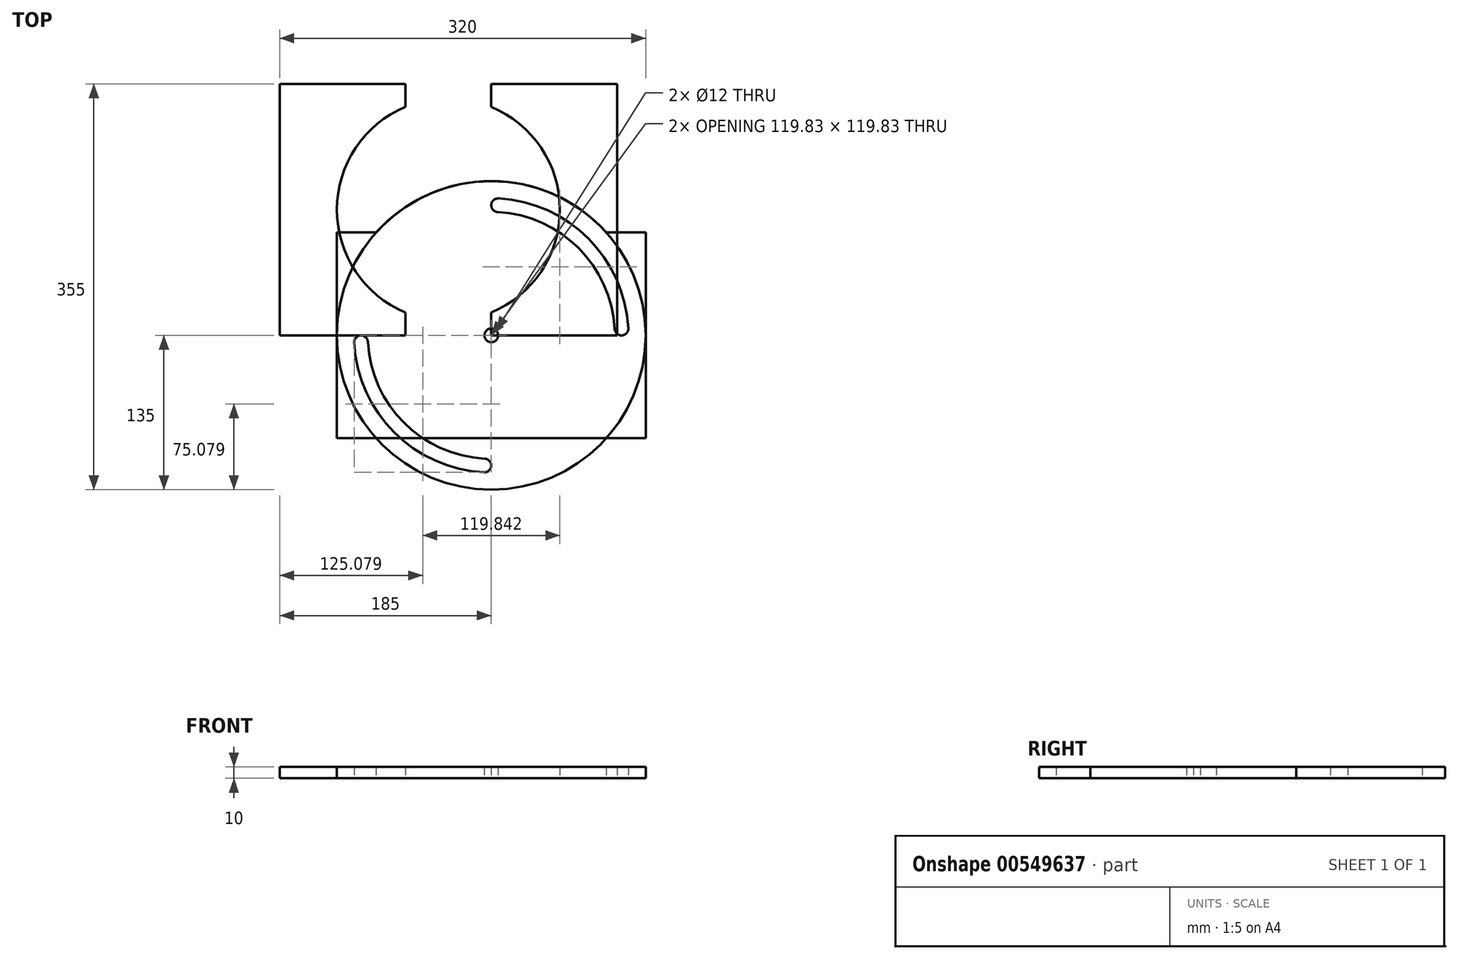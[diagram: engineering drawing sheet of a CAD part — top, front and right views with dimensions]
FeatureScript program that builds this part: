
annotation { "Feature Type Name" : "Feature", "Feature Type Description" : "" }
export const myFeature = defineFeature(function(context is Context, id is Id, definition is map)
    precondition{}
    {
        {
            var Q0;
            Q0=qCreatedBy(makeId("Top.planeOp"),FACE);
            var sketch = newSketch(context, id + "F0", { "sketchPlane" : qUnion([Q0])});
            skLineSegment(sketch, "E0.bottom", {"start": v(0, 0) * mm, "end": v(110, 0) * mm});
            skLineSegment(sketch, "E0.top", {"start": v(0, 220) * mm, "end": v(110, 220) * mm});
            skLineSegment(sketch, "E0.left", {"start": v(0, 0) * mm, "end": v(0, 220) * mm});
            skLineSegment(sketch, "E0.right", {"start": v(110, 0) * mm, "end": v(110, 220) * mm});
            skCircle(sketch, "E1", {"center": v(-37.5, 110) * mm, "radius": 97.5 * mm});
            skLineSegment(sketch, "E2", {"start": v(-37.5, 110) * mm, "end": v(-37.5, 222.8) * mm, "construction": true});
            skLineSegment(sketch, "E3.MirrorCS", {"start": v(-75, 220) * mm, "end": v(-185, 220) * mm});
            skLineSegment(sketch, "E4.MirrorCS", {"start": v(-75, 0) * mm, "end": v(-75, 220) * mm});
            skLineSegment(sketch, "E5.MirrorCS", {"start": v(-75, 0) * mm, "end": v(-185, 0) * mm});
            skLineSegment(sketch, "E6.MirrorCS", {"start": v(-185, 0) * mm, "end": v(-185, 220) * mm});
            skSolve(sketch);
        }
        {
            var Q0;
            {var subQ4=sQuery(id+"F0.wireOp",EDGE,"E0.bottom");Q0=makeQuery(id+"F0.imprint","IMPRINT",FACE,{"disambiguationData":[TD([[makeQuery(id+"F0.imprint","IMPRINT",EDGE,{"derivedFrom":subQ4}),1.0]])]});}
            var Q1;
            {var subQ1=sQuery(id+"F0.wireOp",EDGE,"E3.MirrorCS");Q1=makeQuery(id+"F0.imprint","IMPRINT",FACE,{"disambiguationData":[TD([[makeQuery(id+"F0.imprint","IMPRINT",EDGE,{"derivedFrom":subQ1}),1.0]])]});}
            extrude(context, id + "F1", {"entities" : qUnion([Q0, Q1]), "depth" : 10 * mm, "offsetDistance" : 25 * mm});
        }
        {
            var Q0;
            Q0=qCreatedBy(makeId("Top.planeOp"),FACE);
            var sketch = newSketch(context, id + "F2", { "sketchPlane" : qUnion([Q0])});
            skCircle(sketch, "E7", {"center": v(0, 0) * mm, "radius": 135 * mm});
            skCircle(sketch, "E8", {"center": v(0, 0) * mm, "radius": 6 * mm});
            skArc(sketch, "E9.0", {"start": v(119.83, 6.32) * mm, "mid": v(84.85, 84.85) * mm, "end": v(6.32, 119.83) * mm});
            skArc(sketch, "E10.0", {"start": v(107.85, 5.68) * mm, "mid": v(76.37, 76.37) * mm, "end": v(5.68, 107.85) * mm});
            skLineSegment(sketch, "E11", {"start": v(0, 0) * mm, "end": v(127.14, -127.14) * mm, "construction": true});
            skLineSegment(sketch, "E12.trimOffspring", {"start": v(113.84, 0) * mm, "end": v(113.84, 0) * mm});
            skLineSegment(sketch, "E13.trimOffspring", {"start": v(0, 113.84) * mm, "end": v(0, 113.84) * mm});
            skPoint(sketch, "E14.visualSharp", {"position": v(0, 120) * mm});
            skArc(sketch, "E14.filletArc", {"start": v(6.32, 119.83) * mm, "mid": v(1.87, 118.2) * mm, "end": v(0, 113.84) * mm});
            skLineSegment(sketch, "E15", {"start": v(0, 0) * mm, "end": v(108, 0) * mm, "construction": true});
            skLineSegment(sketch, "E16", {"start": v(0, 108) * mm, "end": v(0, 0) * mm, "construction": true});
            skPoint(sketch, "E17.visualSharp", {"position": v(0, 108) * mm});
            skArc(sketch, "E17.filletArc", {"start": v(0, 113.84) * mm, "mid": v(1.65, 109.71) * mm, "end": v(5.68, 107.85) * mm});
            skPoint(sketch, "E18.visualSharp", {"position": v(120, 0) * mm});
            skArc(sketch, "E18.filletArc", {"start": v(113.84, 0) * mm, "mid": v(118.2, 1.87) * mm, "end": v(119.83, 6.32) * mm});
            skPoint(sketch, "E19.visualSharp", {"position": v(108, 0) * mm});
            skArc(sketch, "E19.filletArc", {"start": v(107.85, 5.68) * mm, "mid": v(109.71, 1.65) * mm, "end": v(113.84, 0) * mm});
            skArc(sketch, "E20.MirrorCS", {"start": v(-5.68, -107.85) * mm, "mid": v(-76.37, -76.37) * mm, "end": v(-107.85, -5.68) * mm});
            skArc(sketch, "E21.MirrorCS", {"start": v(-6.32, -119.83) * mm, "mid": v(-84.85, -84.85) * mm, "end": v(-119.83, -6.32) * mm});
            skArc(sketch, "E22.MirrorCS", {"start": v(-119.83, -6.32) * mm, "mid": v(-118.2, -1.87) * mm, "end": v(-113.84, 0) * mm});
            skArc(sketch, "E23.MirrorCS", {"start": v(-113.84, 0) * mm, "mid": v(-109.71, -1.65) * mm, "end": v(-107.85, -5.68) * mm});
            skArc(sketch, "E24.MirrorCS", {"start": v(0, -113.84) * mm, "mid": v(-1.87, -118.2) * mm, "end": v(-6.32, -119.83) * mm});
            skArc(sketch, "E25.MirrorCS", {"start": v(-5.68, -107.85) * mm, "mid": v(-1.65, -109.71) * mm, "end": v(0, -113.84) * mm});
            skSolve(sketch);
        }
        {
            var Q0;
            Q0=makeQuery(id+"F2.imprint","IMPRINT",FACE,{"disambiguationData":[TD([[makeQuery(id+"F2.imprint","IMPRINT",EDGE,{"derivedFrom":sQuery(id+"F2.wireOp",EDGE,"E7")}),1.0]])]});
            extrude(context, id + "F3", {"entities" : qUnion([Q0]), "depth" : 10 * mm, "offsetDistance" : 25 * mm});
        }
        {
            var Q0;
            Q0=qCreatedBy(makeId("Top.planeOp"),FACE);
            var sketch = newSketch(context, id + "F4", { "sketchPlane" : qUnion([Q0])});
            skCircle(sketch, "E26", {"center": v(0, 0) * mm, "radius": 135 * mm});
            skCircle(sketch, "E27", {"center": v(0, 0) * mm, "radius": 6 * mm});
            skLineSegment(sketch, "E28.bottom", {"start": v(135, -90) * mm, "end": v(-135, -90) * mm});
            skLineSegment(sketch, "E28.top", {"start": v(135, 90) * mm, "end": v(-135, 90) * mm});
            skLineSegment(sketch, "E28.left", {"start": v(135, -90) * mm, "end": v(135, 90) * mm});
            skLineSegment(sketch, "E28.right", {"start": v(-135, -90) * mm, "end": v(-135, 90) * mm});
            skSolve(sketch);
        }
        {
            var Q0;
            Q0=makeQuery(id+"F4.imprint","IMPRINT",FACE,{"disambiguationData":[TD([[makeQuery(id+"F4.imprint","IMPRINT",EDGE,{"derivedFrom":sQuery(id+"F4.wireOp",EDGE,"E27")}),-1.0]])]});
            var Q1;
            {var subQ0=sQuery(id+"F4.wireOp",EDGE,"E28.top");var subQ1=sQuery(id+"F4.wireOp",EDGE,"E26");var subQ2=makeQuery(id+"F4.imprint","INTERSECT",VERTEX,{"disambiguationData":[OD(0.0)],"derivedFrom":[subQ1,subQ0]});Q1=makeQuery(id+"F4.imprint","IMPRINT",FACE,{"disambiguationData":[TD([[makeQuery(id+"F4.imprint","IMPRINT",EDGE,{"disambiguationData":[TD([[subQ2,-1.0]])],"derivedFrom":subQ1}),1.0]])]});}
            var Q2;
            {var subQ0=sQuery(id+"F4.wireOp",EDGE,"E28.top");var subQ1=sQuery(id+"F4.wireOp",EDGE,"E26");var subQ2=makeQuery(id+"F4.imprint","INTERSECT",VERTEX,{"disambiguationData":[OD(0.0)],"derivedFrom":[subQ1,subQ0]});Q2=makeQuery(id+"F4.imprint","IMPRINT",FACE,{"disambiguationData":[TD([[makeQuery(id+"F4.imprint","IMPRINT",EDGE,{"disambiguationData":[TD([[subQ2,1.0]])],"derivedFrom":subQ1}),-1.0]])]});}
            var Q3;
            {var subQ0=sQuery(id+"F4.wireOp",EDGE,"E28.left");var subQ1=sQuery(id+"F4.wireOp",EDGE,"E26");var subQ2=makeQuery(id+"F4.imprint","INTERSECT",VERTEX,{"derivedFrom":[subQ1,subQ0]});Q3=makeQuery(id+"F4.imprint","IMPRINT",FACE,{"disambiguationData":[TD([[makeQuery(id+"F4.imprint","IMPRINT",EDGE,{"disambiguationData":[TD([[subQ2,1.0]])],"derivedFrom":subQ1}),-1.0]])]});}
            var Q4;
            {var subQ0=sQuery(id+"F4.wireOp",EDGE,"E28.bottom");var subQ1=sQuery(id+"F4.wireOp",EDGE,"E26");var subQ2=makeQuery(id+"F4.imprint","INTERSECT",VERTEX,{"disambiguationData":[OD(0.0)],"derivedFrom":[subQ1,subQ0]});Q4=makeQuery(id+"F4.imprint","IMPRINT",FACE,{"disambiguationData":[TD([[makeQuery(id+"F4.imprint","IMPRINT",EDGE,{"disambiguationData":[TD([[subQ2,-1.0]])],"derivedFrom":subQ1}),1.0]])]});}
            var Q5;
            {var subQ0=sQuery(id+"F4.wireOp",EDGE,"E28.right");var subQ1=sQuery(id+"F4.wireOp",EDGE,"E26");var subQ2=makeQuery(id+"F4.imprint","INTERSECT",VERTEX,{"derivedFrom":[subQ1,subQ0]});Q5=makeQuery(id+"F4.imprint","IMPRINT",FACE,{"disambiguationData":[TD([[makeQuery(id+"F4.imprint","IMPRINT",EDGE,{"disambiguationData":[TD([[subQ2,-1.0]])],"derivedFrom":subQ1}),-1.0]])]});}
            var Q6;
            {var subQ0=sQuery(id+"F4.wireOp",EDGE,"E28.top");var subQ1=sQuery(id+"F4.wireOp",EDGE,"E26");var subQ2=makeQuery(id+"F4.imprint","INTERSECT",VERTEX,{"disambiguationData":[OD(1.0)],"derivedFrom":[subQ1,subQ0]});Q6=makeQuery(id+"F4.imprint","IMPRINT",FACE,{"disambiguationData":[TD([[makeQuery(id+"F4.imprint","IMPRINT",EDGE,{"disambiguationData":[TD([[subQ2,-1.0]])],"derivedFrom":subQ1}),-1.0]])]});}
            extrude(context, id + "F5", {"entities" : qUnion([Q0, Q1, Q2, Q3, Q4, Q5, Q6]), "depth" : 10 * mm, "offsetDistance" : 25 * mm});
        }
    });
